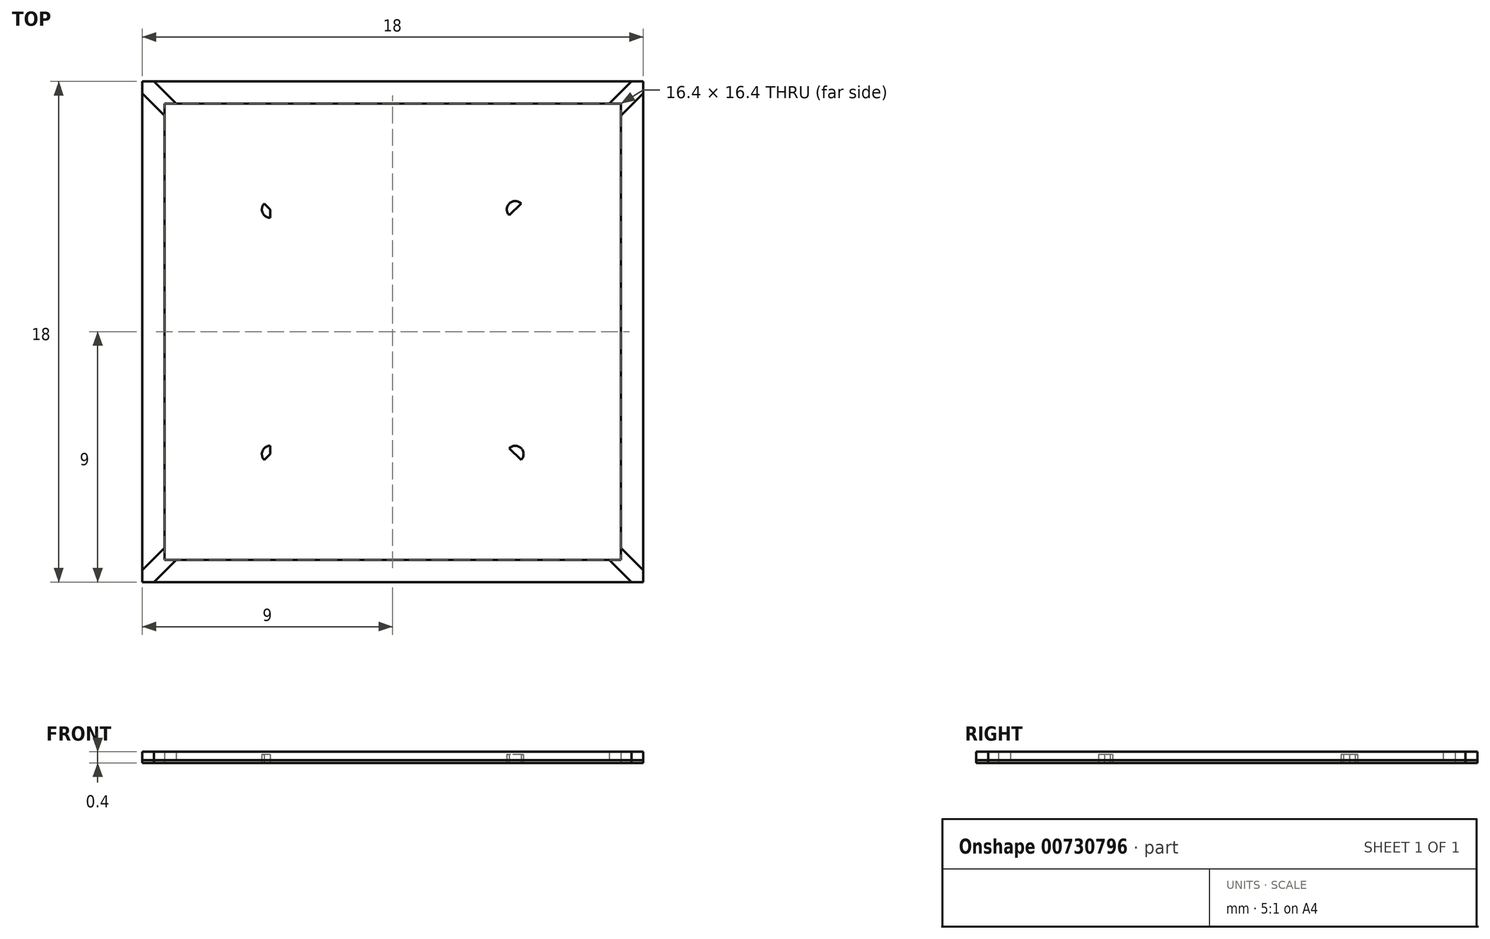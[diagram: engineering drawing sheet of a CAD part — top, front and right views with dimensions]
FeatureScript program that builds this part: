
annotation { "Feature Type Name" : "Feature", "Feature Type Description" : "" }
export const myFeature = defineFeature(function(context is Context, id is Id, definition is map)
    precondition{}
    {
        {
            var Q0;
            Q0=qCreatedBy(makeId("Top.planeOp"),FACE);
            var sketch = newSketch(context, id + "F0", { "sketchPlane" : qUnion([Q0])});
            skLineSegment(sketch, "E0.bottom", {"start": v(5, 5) * mm, "end": v(-5, 5) * mm});
            skLineSegment(sketch, "E0.top", {"start": v(5, -5) * mm, "end": v(-5, -5) * mm});
            skLineSegment(sketch, "E0.left", {"start": v(5, 5) * mm, "end": v(5, -5) * mm});
            skLineSegment(sketch, "E0.right", {"start": v(-5, 5) * mm, "end": v(-5, -5) * mm});
            skPoint(sketch, "E0.middle", {"position": v(0, 0) * mm});
            skLineSegment(sketch, "E1.0", {"start": v(-4.4, 4.4) * mm, "end": v(-4.4, -4.4) * mm});
            skLineSegment(sketch, "E1.1", {"start": v(4.4, 4.4) * mm, "end": v(-4.4, 4.4) * mm});
            skLineSegment(sketch, "E1.2", {"start": v(4.4, 4.4) * mm, "end": v(4.4, -4.4) * mm});
            skLineSegment(sketch, "E1.3", {"start": v(4.4, -4.4) * mm, "end": v(-4.4, -4.4) * mm});
            skCircle(sketch, "E2", {"center": v(-4.4, -4.4) * mm, "radius": 0.3 * mm});
            skCircle(sketch, "E3", {"center": v(4.4, -4.4) * mm, "radius": 0.3 * mm});
            skCircle(sketch, "E4", {"center": v(4.4, 4.4) * mm, "radius": 0.3 * mm});
            skCircle(sketch, "E5", {"center": v(-4.4, 4.4) * mm, "radius": 0.3 * mm});
            skLineSegment(sketch, "E6.bottom", {"start": v(9, -9) * mm, "end": v(-9, -9) * mm});
            skLineSegment(sketch, "E6.top", {"start": v(9, 9) * mm, "end": v(-9, 9) * mm});
            skLineSegment(sketch, "E6.left", {"start": v(9, -9) * mm, "end": v(9, 9) * mm});
            skLineSegment(sketch, "E6.right", {"start": v(-9, -9) * mm, "end": v(-9, 9) * mm});
            skLineSegment(sketch, "E7.0", {"start": v(-8.2, -8.2) * mm, "end": v(-8.2, 8.2) * mm});
            skLineSegment(sketch, "E7.1", {"start": v(8.2, -8.2) * mm, "end": v(-8.2, -8.2) * mm});
            skLineSegment(sketch, "E7.2", {"start": v(8.2, -8.2) * mm, "end": v(8.2, 8.2) * mm});
            skLineSegment(sketch, "E7.3", {"start": v(8.2, 8.2) * mm, "end": v(-8.2, 8.2) * mm});
            skLineSegment(sketch, "E8", {"start": v(-9, 9) * mm, "end": v(9, -9) * mm});
            skLineSegment(sketch, "E9", {"start": v(9, 9) * mm, "end": v(-9, -9) * mm});
            skLineSegment(sketch, "E10.0", {"start": v(8.79, 9.21) * mm, "end": v(-9.21, -8.79) * mm});
            skLineSegment(sketch, "E11.0", {"start": v(9.21, 8.79) * mm, "end": v(-8.79, -9.21) * mm});
            skLineSegment(sketch, "E12.0", {"start": v(-9.21, 8.79) * mm, "end": v(8.79, -9.21) * mm});
            skLineSegment(sketch, "E13.0", {"start": v(-8.79, 9.21) * mm, "end": v(9.21, -8.79) * mm});
            skSolve(sketch);
        }
        {
            var Q0;
            Q0 = qSketchRegion(id + "F0", true);
            extrude(context, id + "F1", {"entities" : qUnion([Q0]), "depth" : .1 * mm, "offsetDistance" : 25 * mm});
        }
        {
            var Q0;
            Q0=makeQuery(id+"F0.imprint","IMPRINT",FACE,{"disambiguationData":[TD([[makeQuery(id+"F0.imprint","IMPRINT",EDGE,{"derivedFrom":sQuery(id+"F0.wireOp",EDGE,"E1.0")}),1.0]])]});
            var sketch = newSketch(context, id + "F2", { "sketchPlane" : qUnion([Q0])});
            skSolve(sketch);
        }
        {
            var Q0;
            {var subQ0=sQuery(id+"F0.wireOp",EDGE,"E1.1");var subQ1=sQuery(id+"F0.wireOp",EDGE,"E1.0");var subQ2=makeQuery(id+"F0.imprint","INTERSECT",VERTEX,{"derivedFrom":[subQ1,subQ0]});Q0=makeQuery(id+"F0.imprint","IMPRINT",FACE,{"disambiguationData":[TD([[makeQuery(id+"F0.imprint","IMPRINT",EDGE,{"disambiguationData":[TD([[subQ2,-1.0]])],"derivedFrom":subQ1}),-1.0]])]});}
            var Q1;
            {var subQ0=sQuery(id+"F0.wireOp",EDGE,"E1.1");var subQ1=sQuery(id+"F0.wireOp",EDGE,"E1.0");var subQ2=makeQuery(id+"F0.imprint","INTERSECT",VERTEX,{"derivedFrom":[subQ1,subQ0]});Q1=makeQuery(id+"F2.imprint","IMPRINT",FACE,{"disambiguationData":[TD([[makeQuery(id+"F2.imprint","IMPRINT",EDGE,{"derivedFrom":makeQuery(id+"F0.imprint","IMPRINT",EDGE,{"disambiguationData":[TD([[subQ2,-1.0]])],"derivedFrom":subQ1})}),1.0]])]});}
            var Q2;
            {var subQ0=sQuery(id+"F0.wireOp",EDGE,"E1.2");var subQ1=sQuery(id+"F0.wireOp",EDGE,"E1.1");var subQ2=makeQuery(id+"F0.imprint","INTERSECT",VERTEX,{"derivedFrom":[subQ1,subQ0]});Q2=makeQuery(id+"F0.imprint","IMPRINT",FACE,{"disambiguationData":[TD([[makeQuery(id+"F0.imprint","IMPRINT",EDGE,{"disambiguationData":[TD([[subQ2,-1.0]])],"derivedFrom":subQ1}),1.0]])]});}
            var Q3;
            {var subQ0=sQuery(id+"F0.wireOp",EDGE,"E1.2");var subQ1=sQuery(id+"F0.wireOp",EDGE,"E1.1");var subQ2=makeQuery(id+"F0.imprint","INTERSECT",VERTEX,{"derivedFrom":[subQ1,subQ0]});Q3=makeQuery(id+"F0.imprint","IMPRINT",FACE,{"disambiguationData":[TD([[makeQuery(id+"F0.imprint","IMPRINT",EDGE,{"disambiguationData":[TD([[subQ2,-1.0]])],"derivedFrom":subQ1}),-1.0]])]});}
            var Q4;
            {var subQ0=sQuery(id+"F0.wireOp",EDGE,"E1.3");var subQ1=sQuery(id+"F0.wireOp",EDGE,"E1.2");var subQ2=makeQuery(id+"F0.imprint","INTERSECT",VERTEX,{"derivedFrom":[subQ1,subQ0]});Q4=makeQuery(id+"F0.imprint","IMPRINT",FACE,{"disambiguationData":[TD([[makeQuery(id+"F0.imprint","IMPRINT",EDGE,{"disambiguationData":[TD([[subQ2,1.0]])],"derivedFrom":subQ1}),1.0]])]});}
            var Q5;
            {var subQ0=sQuery(id+"F0.wireOp",EDGE,"E1.3");var subQ1=sQuery(id+"F0.wireOp",EDGE,"E1.2");var subQ2=makeQuery(id+"F0.imprint","INTERSECT",VERTEX,{"derivedFrom":[subQ1,subQ0]});Q5=makeQuery(id+"F0.imprint","IMPRINT",FACE,{"disambiguationData":[TD([[makeQuery(id+"F0.imprint","IMPRINT",EDGE,{"disambiguationData":[TD([[subQ2,1.0]])],"derivedFrom":subQ1}),-1.0]])]});}
            var Q6;
            {var subQ0=sQuery(id+"F0.wireOp",EDGE,"E1.3");var subQ1=sQuery(id+"F0.wireOp",EDGE,"E1.0");var subQ2=makeQuery(id+"F0.imprint","INTERSECT",VERTEX,{"derivedFrom":[subQ1,subQ0]});Q6=makeQuery(id+"F2.imprint","IMPRINT",FACE,{"disambiguationData":[TD([[makeQuery(id+"F2.imprint","IMPRINT",EDGE,{"derivedFrom":makeQuery(id+"F0.imprint","IMPRINT",EDGE,{"disambiguationData":[TD([[subQ2,1.0]])],"derivedFrom":subQ1})}),1.0]])]});}
            var Q7;
            {var subQ0=sQuery(id+"F0.wireOp",EDGE,"E1.3");var subQ1=sQuery(id+"F0.wireOp",EDGE,"E1.0");var subQ2=makeQuery(id+"F0.imprint","INTERSECT",VERTEX,{"derivedFrom":[subQ1,subQ0]});Q7=makeQuery(id+"F0.imprint","IMPRINT",FACE,{"disambiguationData":[TD([[makeQuery(id+"F0.imprint","IMPRINT",EDGE,{"disambiguationData":[TD([[subQ2,1.0]])],"derivedFrom":subQ1}),-1.0]])]});}
            extrude(context, id + "F3", {"entities" : qUnion([Q0, Q1, Q2, Q3, Q4, Q5, Q6, Q7]), "depth" : .3 * mm, "offsetDistance" : 25 * mm});
        }
        {
            var Q0;
            {var subQ0=sQuery(id+"F0.wireOp",EDGE,"E10.0");var subQ1=sQuery(id+"F0.wireOp",EDGE,"E6.right");var subQ2=makeQuery(id+"F0.imprint","INTERSECT",VERTEX,{"derivedFrom":[subQ1,subQ0]});Q0=makeQuery(id+"F0.imprint","IMPRINT",FACE,{"disambiguationData":[TD([[makeQuery(id+"F0.imprint","IMPRINT",EDGE,{"disambiguationData":[TD([[subQ2,-1.0]])],"derivedFrom":subQ1}),-1.0]])]});}
            var Q1;
            {var subQ0=sQuery(id+"F0.wireOp",EDGE,"E10.0");var subQ1=sQuery(id+"F0.wireOp",EDGE,"E6.top");var subQ2=makeQuery(id+"F0.imprint","INTERSECT",VERTEX,{"derivedFrom":[subQ1,subQ0]});Q1=makeQuery(id+"F0.imprint","IMPRINT",FACE,{"disambiguationData":[TD([[makeQuery(id+"F0.imprint","IMPRINT",EDGE,{"disambiguationData":[TD([[subQ2,-1.0]])],"derivedFrom":subQ1}),1.0]])]});}
            var Q2;
            {var subQ0=sQuery(id+"F0.wireOp",EDGE,"E13.0");var subQ1=sQuery(id+"F0.wireOp",EDGE,"E6.left");var subQ2=makeQuery(id+"F0.imprint","INTERSECT",VERTEX,{"derivedFrom":[subQ1,subQ0]});Q2=makeQuery(id+"F0.imprint","IMPRINT",FACE,{"disambiguationData":[TD([[makeQuery(id+"F0.imprint","IMPRINT",EDGE,{"disambiguationData":[TD([[subQ2,-1.0]])],"derivedFrom":subQ1}),1.0]])]});}
            var Q3;
            {var subQ0=sQuery(id+"F0.wireOp",EDGE,"E12.0");var subQ1=sQuery(id+"F0.wireOp",EDGE,"E6.bottom");var subQ2=makeQuery(id+"F0.imprint","INTERSECT",VERTEX,{"derivedFrom":[subQ1,subQ0]});Q3=makeQuery(id+"F0.imprint","IMPRINT",FACE,{"disambiguationData":[TD([[makeQuery(id+"F0.imprint","IMPRINT",EDGE,{"disambiguationData":[TD([[subQ2,-1.0]])],"derivedFrom":subQ1}),-1.0]])]});}
            extrude(context, id + "F4", {"entities" : qUnion([Q0, Q1, Q2, Q3]), "depth" : .4 * mm, "offsetDistance" : 25 * mm});
        }
    });
